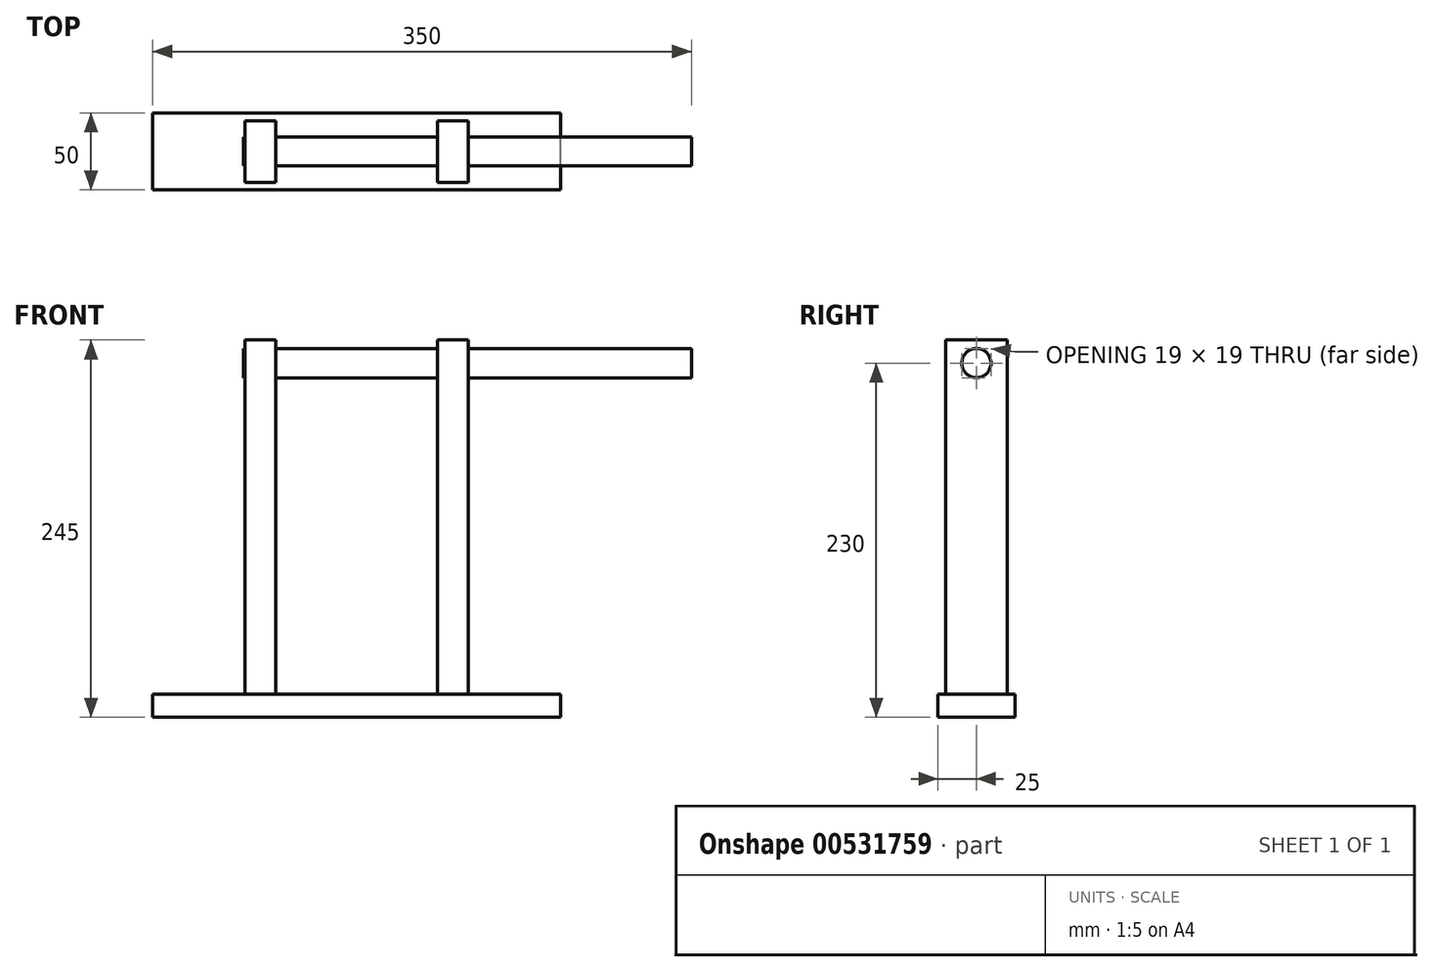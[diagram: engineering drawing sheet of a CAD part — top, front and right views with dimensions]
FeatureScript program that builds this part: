
annotation { "Feature Type Name" : "Feature", "Feature Type Description" : "" }
export const myFeature = defineFeature(function(context is Context, id is Id, definition is map)
    precondition{}
    {
        {
            var Q0;
            Q0=qCreatedBy(makeId("Right.planeOp"),FACE);
            var sketch = newSketch(context, id + "F0", { "sketchPlane" : qUnion([Q0])});
            skCircle(sketch, "E0", {"center": v(0, 0) * mm, "radius": 9.5 * mm});
            skSolve(sketch);
        }
        {
            var Q0;
            Q0 = qSketchRegion(id + "F0", true);
            var Q1;
            Q1=makeQuery(id+"F0.imprint","IMPRINT",FACE,{"disambiguationData":[TD([[makeQuery(id+"F0.imprint","IMPRINT",EDGE,{"derivedFrom":sQuery(id+"F0.wireOp",EDGE,"E0")}),1.0]])]});
            extrude(context, id + "F1", {"entities" : qUnion([Q0, Q1]), "oppositeDirection" : true, "depth" : 40 * mm, "offsetDistance" : 25 * mm});
        }
        {
            var Q0;
            Q0=makeQuery(id+"F1.opExtrude","CAP_FACE",FACE,{"disambiguationData":[OSD([sQuery(id+"F0.wireOp",EDGE,"E0")])],"isStart":true});
            var sketch = newSketch(context, id + "F2", { "sketchPlane" : qUnion([Q0])});
            skCircle(sketch, "E1", {"center": v(0, 0) * mm, "radius": 9.5 * mm});
            skSolve(sketch);
        }
        {
            var Q0;
            Q0 = qSketchRegion(id + "F2", true);
            var Q1;
            Q1=makeQuery(id+"F2.imprint","IMPRINT",FACE,{"disambiguationData":[TD([[makeQuery(id+"F2.imprint","IMPRINT",EDGE,{"derivedFrom":sQuery(id+"F2.wireOp",EDGE,"E1")}),1.0]])]});
            extrude(context, id + "F3", {"entities" : qUnion([Q0, Q1]), "operationType" : NewBodyOperationType.ADD, "depth" : 70 * mm, "offsetDistance" : 25 * mm});
        }
        {
            var Q0;
            Q0=makeQuery(id+"F3.opExtrude","CAP_FACE",FACE,{"disambiguationData":[OSD([sQuery(id+"F2.wireOp",EDGE,"E1")])],"isStart":false});
            var sketch = newSketch(context, id + "F4", { "sketchPlane" : qUnion([Q0])});
            skCircle(sketch, "E2", {"center": v(0, 0) * mm, "radius": 9.5 * mm});
            skSolve(sketch);
        }
        {
            var Q0;
            Q0 = qSketchRegion(id + "F4", true);
            extrude(context, id + "F5", {"entities" : qUnion([Q0]), "operationType" : NewBodyOperationType.ADD, "depth" : 180 * mm, "offsetDistance" : 25 * mm});
        }
        {
            var Q0;
            Q0=qCreatedBy(makeId("Top.planeOp"),FACE);
            var sketch = newSketch(context, id + "F6", { "sketchPlane" : qUnion([Q0])});
            skLineSegment(sketch, "E3", {"start": v(0, 0) * mm, "end": v(-40, 0) * mm});
            skLineSegment(sketch, "E4", {"start": v(-40, 0) * mm, "end": v(-20, 0) * mm});
            skPoint(sketch, "E5.start.orphan", {"position": v(-40, 10) * mm});
            skPoint(sketch, "E6.start.orphan", {"position": v(-20, -10) * mm});
            skLineSegment(sketch, "E7", {"start": v(-20, 0) * mm, "end": v(-20, 20) * mm});
            skLineSegment(sketch, "E8", {"start": v(-20, 20) * mm, "end": v(-40, 20) * mm});
            skLineSegment(sketch, "E9", {"start": v(-40, 20) * mm, "end": v(-40, -20) * mm});
            skLineSegment(sketch, "E10", {"start": v(-40, -20) * mm, "end": v(-20, -20) * mm});
            skLineSegment(sketch, "E11", {"start": v(-20, -20) * mm, "end": v(-20, 0) * mm});
            skSolve(sketch);
        }
        {
            var Q0;
            Q0 = qSketchRegion(id + "F6", true);
            extrude(context, id + "F7", {"entities" : qUnion([Q0]), "operationType" : NewBodyOperationType.ADD, "depth" : 15 * mm, "offsetDistance" : 25 * mm});
        }
        {
            var Q0;
            Q0=qCreatedBy(makeId("Top.planeOp"),FACE);
            var sketch = newSketch(context, id + "F8", { "sketchPlane" : qUnion([Q0])});
            skLineSegment(sketch, "E12", {"start": v(0, 0) * mm, "end": v(-40, 0) * mm});
            skLineSegment(sketch, "E13", {"start": v(-40, 0) * mm, "end": v(-40, -10) * mm});
            skLineSegment(sketch, "E14", {"start": v(-40, -10) * mm, "end": v(-20, -10) * mm});
            skLineSegment(sketch, "E15", {"start": v(-20, -10) * mm, "end": v(-20, 10) * mm});
            skLineSegment(sketch, "E16", {"start": v(-20, 10) * mm, "end": v(-40, 10) * mm});
            skLineSegment(sketch, "E17", {"start": v(-40, 10) * mm, "end": v(-40, 0) * mm});
            skLineSegment(sketch, "E18", {"start": v(-20, -10) * mm, "end": v(-20, -20) * mm});
            skLineSegment(sketch, "E19", {"start": v(-20, -20) * mm, "end": v(-40, -20) * mm});
            skLineSegment(sketch, "E20", {"start": v(-40, -20) * mm, "end": v(-40, 20) * mm});
            skLineSegment(sketch, "E21", {"start": v(-40, 20) * mm, "end": v(-20, 20) * mm});
            skLineSegment(sketch, "E22", {"start": v(-20, 20) * mm, "end": v(-20, 10) * mm});
            skSolve(sketch);
        }
        {
            var Q0;
            Q0 = qSketchRegion(id + "F8", true);
            extrude(context, id + "F9", {"entities" : qUnion([Q0]), "operationType" : NewBodyOperationType.ADD, "oppositeDirection" : true, "depth" : 215 * mm, "offsetDistance" : 25 * mm});
        }
        {
            var Q0;
            Q0=qCreatedBy(makeId("Top.planeOp"),FACE);
            var sketch = newSketch(context, id + "F10", { "sketchPlane" : qUnion([Q0])});
            skLineSegment(sketch, "E23", {"start": v(0, 0) * mm, "end": v(70, 0) * mm});
            skLineSegment(sketch, "E24", {"start": v(70, 0) * mm, "end": v(85, 0) * mm});
            skLineSegment(sketch, "E25", {"start": v(85, 0) * mm, "end": v(85, -10) * mm});
            skLineSegment(sketch, "E26", {"start": v(85, 10) * mm, "end": v(85, 0) * mm});
            skLineSegment(sketch, "E27", {"start": v(85, -10) * mm, "end": v(85, -20) * mm});
            skLineSegment(sketch, "E28", {"start": v(85, -20) * mm, "end": v(105, -20) * mm});
            skLineSegment(sketch, "E29", {"start": v(105, -20) * mm, "end": v(105, 20) * mm});
            skLineSegment(sketch, "E30", {"start": v(105, 20) * mm, "end": v(85, 20) * mm});
            skLineSegment(sketch, "E31", {"start": v(85, 20) * mm, "end": v(85, 10) * mm});
            skSolve(sketch);
        }
        {
            var Q0;
            Q0 = qSketchRegion(id + "F10", true);
            extrude(context, id + "F11", {"entities" : qUnion([Q0]), "operationType" : NewBodyOperationType.ADD, "depth" : 15 * mm, "offsetDistance" : 25 * mm});
        }
        {
            var Q0;
            Q0 = qSketchRegion(id + "F6", true);
            extrude(context, id + "F12", {"entities" : qUnion([Q0]), "operationType" : NewBodyOperationType.ADD, "depth" : 15 * mm, "offsetDistance" : 25 * mm});
        }
        {
            var Q0;
            Q0 = qSketchRegion(id + "F8", true);
            extrude(context, id + "F13", {"entities" : qUnion([Q0]), "operationType" : NewBodyOperationType.ADD, "oppositeDirection" : true, "depth" : 215 * mm, "offsetDistance" : 25 * mm});
        }
        {
            var Q0;
            Q0=qCreatedBy(makeId("Top.planeOp"),FACE);
            var sketch = newSketch(context, id + "F14", { "sketchPlane" : qUnion([Q0])});
            skLineSegment(sketch, "E32", {"start": v(0, 0) * mm, "end": v(70, 0) * mm});
            skLineSegment(sketch, "E33", {"start": v(70, 0) * mm, "end": v(85, 0) * mm});
            skLineSegment(sketch, "E34", {"start": v(85, 0) * mm, "end": v(85, 20) * mm});
            skLineSegment(sketch, "E35", {"start": v(85, 20) * mm, "end": v(105, 20) * mm});
            skLineSegment(sketch, "E36", {"start": v(105, 20) * mm, "end": v(105, -20) * mm});
            skLineSegment(sketch, "E37", {"start": v(105, -20) * mm, "end": v(85, -20) * mm});
            skLineSegment(sketch, "E38", {"start": v(85, -20) * mm, "end": v(85, 0) * mm});
            skSolve(sketch);
        }
        {
            var Q0;
            Q0 = qSketchRegion(id + "F14", true);
            extrude(context, id + "F15", {"entities" : qUnion([Q0]), "operationType" : NewBodyOperationType.ADD, "oppositeDirection" : true, "depth" : 215 * mm, "offsetDistance" : 25 * mm});
        }
        {
            var Q0;
            Q0=qCreatedBy(makeId("Front.planeOp"),FACE);
            var sketch = newSketch(context, id + "F16", { "sketchPlane" : qUnion([Q0])});
            skLineSegment(sketch, "E39", {"start": v(0, -215) * mm, "end": v(-40, -215) * mm});
            skLineSegment(sketch, "E40", {"start": v(-40, -215) * mm, "end": v(-100, -215) * mm});
            skLineSegment(sketch, "E41", {"start": v(-100, -215) * mm, "end": v(-100, -230) * mm});
            skLineSegment(sketch, "E42", {"start": v(-100, -230) * mm, "end": v(165, -230) * mm});
            skLineSegment(sketch, "E43", {"start": v(165, -230) * mm, "end": v(165, -215) * mm});
            skLineSegment(sketch, "E44", {"start": v(165, -215) * mm, "end": v(0, -215) * mm});
            skLineSegment(sketch, "E45", {"start": v(-40, -215) * mm, "end": v(-40, -230) * mm});
            skLineSegment(sketch, "E46", {"start": v(-20, -215) * mm, "end": v(-20, -222.5) * mm});
            skLineSegment(sketch, "E47", {"start": v(-20, -222.5) * mm, "end": v(-40, -222.5) * mm});
            skLineSegment(sketch, "E48", {"start": v(-20, -222.5) * mm, "end": v(85, -222.5) * mm});
            skLineSegment(sketch, "E49", {"start": v(85, -222.5) * mm, "end": v(85, -215) * mm});
            skLineSegment(sketch, "E50", {"start": v(85, -215) * mm, "end": v(105, -215) * mm});
            skLineSegment(sketch, "E51", {"start": v(105, -215) * mm, "end": v(105, -222.5) * mm});
            skLineSegment(sketch, "E52", {"start": v(105, -222.5) * mm, "end": v(85, -222.5) * mm});
            skSolve(sketch);
        }
        {
            var Q0;
            {var subQ3=sQuery(id+"F16.wireOp",EDGE,"E46");Q0=makeQuery(id+"F16.imprint","IMPRINT",FACE,{"disambiguationData":[TD([[makeQuery(id+"F16.imprint","IMPRINT",EDGE,{"derivedFrom":subQ3}),-1.0]])]});}
            extrude(context, id + "F17", {"entities" : qUnion([Q0]), "operationType" : NewBodyOperationType.ADD, "depth" : 20 * mm, "offsetDistance" : 25 * mm});
        }
        {
            var Q0;
            Q0 = qSketchRegion(id + "F16", true);
            extrude(context, id + "F18", {"entities" : qUnion([Q0]), "operationType" : NewBodyOperationType.ADD, "depth" : 25 * mm, "offsetDistance" : 25 * mm});
        }
        {
            var Q0;
            Q0 = qSketchRegion(id + "F16", true);
            extrude(context, id + "F19", {"entities" : qUnion([Q0]), "operationType" : NewBodyOperationType.ADD, "oppositeDirection" : true, "depth" : 25 * mm, "offsetDistance" : 25 * mm});
        }
        {
            var Q0;
            Q0=makeQuery(id+"F17.boolean.opBoolean","MERGE",FACE,{"derivedFrom":[makeQuery(id+"F9.boolean.opBoolean","MERGE",FACE,{"derivedFrom":[makeQuery(id+"F7.boolean.opBoolean","MERGE",FACE,{"derivedFrom":[makeQuery(id+"F1.opExtrude","CAP_FACE",FACE,{"disambiguationData":[OSD([sQuery(id+"F0.wireOp",EDGE,"E0")])],"isStart":false}),makeQuery(id+"F7.opExtrude","SWEPT_FACE",FACE,{"disambiguationData":[OSD([sQuery(id+"F6.wireOp",EDGE,"E9")])]})]}),makeQuery(id+"F9.opExtrude","SWEPT_FACE",FACE,{"disambiguationData":[OSD([sQuery(id+"F8.wireOp",EDGE,"E20")])]})]}),makeQuery(id+"F17.opExtrude","SWEPT_FACE",FACE,{"disambiguationData":[OSD([sQuery(id+"F16.wireOp",EDGE,"E45")])]})]});
            var sketch = newSketch(context, id + "F20", { "sketchPlane" : qUnion([Q0])});
            skCircle(sketch, "E53", {"center": v(0, 0) * mm, "radius": 9.5 * mm});
            skSolve(sketch);
        }
        {
            var Q0;
            Q0 = qSketchRegion(id + "F20", true);
            extrude(context, id + "F21", {"entities" : qUnion([Q0]), "operationType" : NewBodyOperationType.ADD, "depth" : 1 * mm, "offsetDistance" : 25 * mm});
        }
    });
